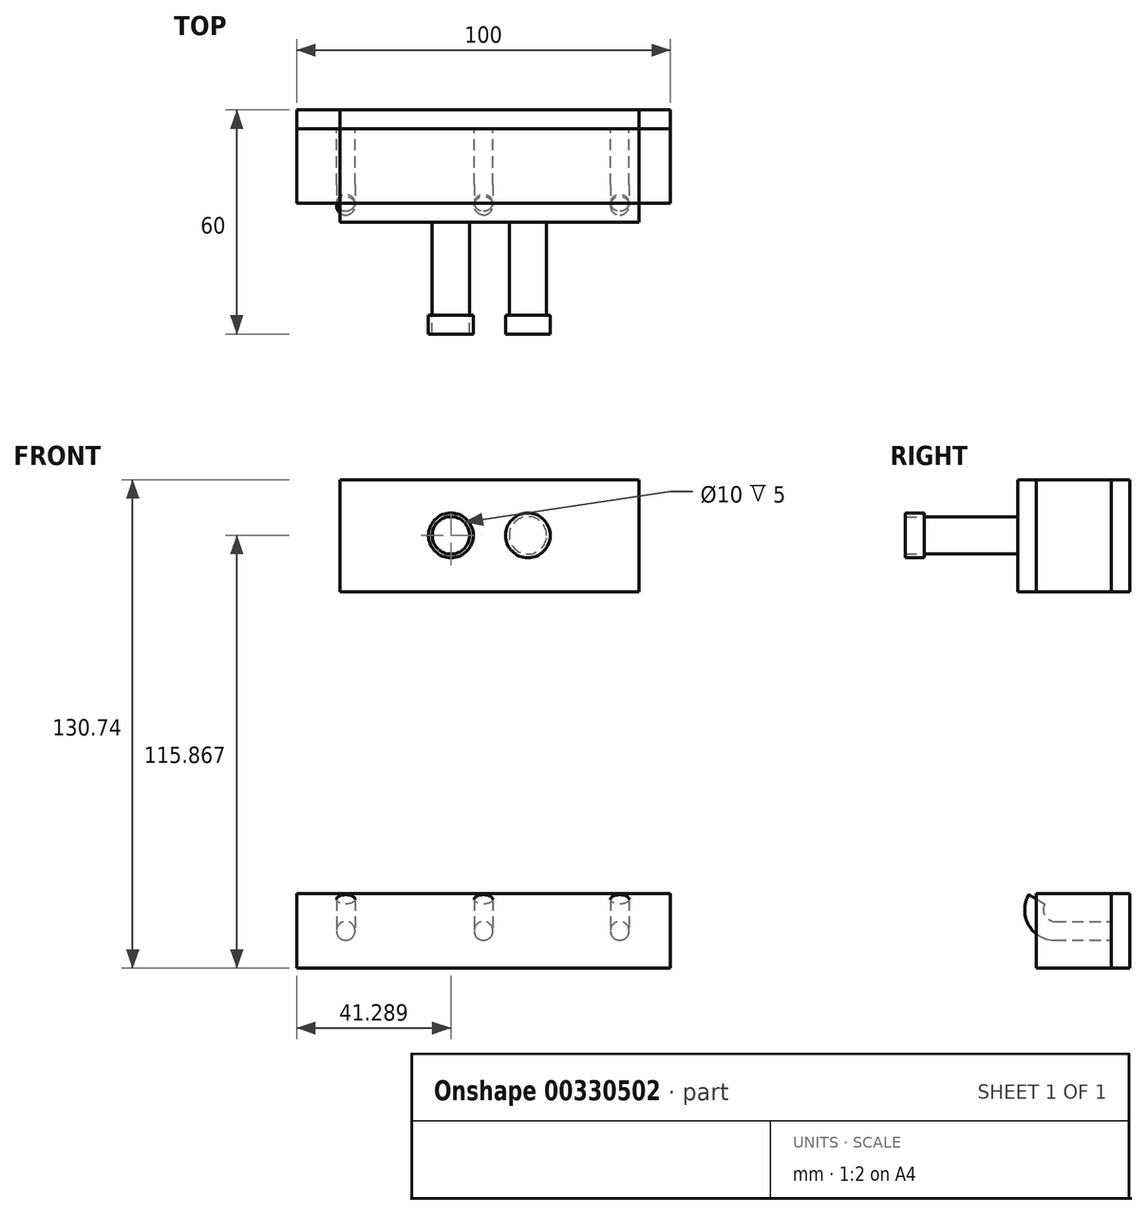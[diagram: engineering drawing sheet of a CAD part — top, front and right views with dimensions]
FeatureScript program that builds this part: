
annotation { "Feature Type Name" : "Feature", "Feature Type Description" : "" }
export const myFeature = defineFeature(function(context is Context, id is Id, definition is map)
    precondition{}
    {
        {
            var Q0;
            Q0=qCreatedBy(makeId("Front.planeOp"),FACE);
            var sketch = newSketch(context, id + "F0", { "sketchPlane" : qUnion([Q0])});
            skLineSegment(sketch, "E0.bottom", {"start": v(50, 10) * mm, "end": v(-50, 10) * mm});
            skLineSegment(sketch, "E0.top", {"start": v(50, -10) * mm, "end": v(-50, -10) * mm});
            skLineSegment(sketch, "E0.left", {"start": v(50, 10) * mm, "end": v(50, -10) * mm});
            skLineSegment(sketch, "E0.right", {"start": v(-50, 10) * mm, "end": v(-50, -10) * mm});
            skPoint(sketch, "E0.middle", {"position": v(0, 0) * mm});
            skLineSegment(sketch, "E1", {"start": v(-38.43, 120.74) * mm, "end": v(41.57, 120.74) * mm});
            skLineSegment(sketch, "E2", {"start": v(41.57, 120.74) * mm, "end": v(41.57, 90.74) * mm});
            skLineSegment(sketch, "E3", {"start": v(41.57, 90.74) * mm, "end": v(-38.43, 90.74) * mm});
            skLineSegment(sketch, "E4", {"start": v(-38.43, 90.74) * mm, "end": v(-38.43, 120.74) * mm});
            skSolve(sketch);
        }
        {
            var Q0;
            Q0 = qSketchRegion(id + "F0", true);
            extrude(context, id + "F1", {"entities" : qUnion([Q0]), "depth" : 5 * mm});
        }
        {
            var Q0;
            Q0=makeQuery(id+"F1.opExtrude","CAP_FACE",FACE,{"disambiguationData":[OSD([sQuery(id+"F0.wireOp",EDGE,"E0.bottom"),sQuery(id+"F0.wireOp",EDGE,"E0.top"),sQuery(id+"F0.wireOp",EDGE,"E0.left"),sQuery(id+"F0.wireOp",EDGE,"E0.right")])],"isStart":false});
            var sketch = newSketch(context, id + "F2", { "sketchPlane" : qUnion([Q0])});
            skCircle(sketch, "E5", {"center": v(0, 0) * mm, "radius": 2.5 * mm});
            skCircle(sketch, "E6", {"center": v(-36.85, 0) * mm, "radius": 2.5 * mm});
            skCircle(sketch, "E7", {"center": v(36.47, 0) * mm, "radius": 2.5 * mm});
            skSolve(sketch);
        }
        {
            var Q0;
            Q0=makeQuery(id+"F2.imprint","IMPRINT",FACE,{"disambiguationData":[TD([[makeQuery(id+"F2.imprint","IMPRINT",EDGE,{"derivedFrom":sQuery(id+"F2.wireOp",EDGE,"E5")}),1.0]])]});
            var Q1;
            Q1=makeQuery(id+"F2.imprint","IMPRINT",FACE,{"disambiguationData":[TD([[makeQuery(id+"F2.imprint","IMPRINT",EDGE,{"derivedFrom":sQuery(id+"F2.wireOp",EDGE,"E6")}),1.0]])]});
            var Q2;
            Q2=makeQuery(id+"F2.imprint","IMPRINT",FACE,{"disambiguationData":[TD([[makeQuery(id+"F2.imprint","IMPRINT",EDGE,{"derivedFrom":sQuery(id+"F2.wireOp",EDGE,"E7")}),1.0]])]});
            var Q3;
            Q3=sQuery(id+"F2.wireOp",EDGE,"E5");
            var Q4;
            Q4=sQuery(id+"F2.wireOp",EDGE,"E6");
            var Q5;
            Q5=sQuery(id+"F2.wireOp",EDGE,"E7");
            extrude(context, id + "F3", {"entities" : qUnion([Q0, Q1, Q2]), "operationType" : NewBodyOperationType.ADD, "surfaceEntities" : qUnion([Q3, Q4, Q5]), "depth" : 15 * mm});
        }
        {
            var Q0;
            Q0=makeQuery(id+"F3.opExtrude","CAP_FACE",FACE,{"disambiguationData":[OSD([sQuery(id+"F2.wireOp",EDGE,"E6")])],"isStart":false});
            var sketch = newSketch(context, id + "F4", { "sketchPlane" : qUnion([Q0])});
            skLineSegment(sketch, "E8", {"start": v(-44.61, 5.63) * mm, "end": v(45.39, 5.63) * mm});
            skSolve(sketch);
        }
        {
            var Q0;
            Q0=makeQuery(id+"F4.imprint","IMPRINT",FACE,{"disambiguationData":[TD([[makeQuery(id+"F4.imprint","IMPRINT",EDGE,{"derivedFrom":makeQuery(id+"F3.opExtrude","CAP_EDGE",EDGE,{"disambiguationData":[OSD([sQuery(id+"F2.wireOp",EDGE,"E6")])],"isStart":false})}),1.0]])]});
            var Q1;
            Q1=makeQuery(id+"F3.opExtrude","CAP_EDGE",EDGE,{"disambiguationData":[OSD([sQuery(id+"F2.wireOp",EDGE,"E6")])],"isStart":false});
            var Q2;
            Q2=sQuery(id+"F4.wireOp",EDGE,"E8");
            revolve(context, id + "F5", {"operationType" : NewBodyOperationType.ADD, "entities" : qUnion([Q0]), "surfaceEntities" : qUnion([Q1]), "axis" : qUnion([Q2]), "revolveType" : RevolveType.ONE_DIRECTION, "oppositeDirection" : true, "angle" : 120 * degree});
        }
        {
            var Q0;
            Q0=makeQuery(id+"F3.opExtrude","CAP_FACE",FACE,{"disambiguationData":[OSD([sQuery(id+"F2.wireOp",EDGE,"E5")])],"isStart":false});
            var Q1;
            Q1=makeQuery(id+"F3.opExtrude","CAP_EDGE",EDGE,{"disambiguationData":[OSD([sQuery(id+"F2.wireOp",EDGE,"E5")])],"isStart":false});
            var Q2;
            Q2=sQuery(id+"F4.wireOp",EDGE,"E8");
            revolve(context, id + "F6", {"operationType" : NewBodyOperationType.ADD, "entities" : qUnion([Q0]), "surfaceEntities" : qUnion([Q1]), "axis" : qUnion([Q2]), "revolveType" : RevolveType.ONE_DIRECTION, "oppositeDirection" : true, "angle" : 120 * degree});
        }
        {
            var Q0;
            Q0=makeQuery(id+"F3.opExtrude","CAP_FACE",FACE,{"disambiguationData":[OSD([sQuery(id+"F2.wireOp",EDGE,"E7")])],"isStart":false});
            var Q1;
            Q1=makeQuery(id+"F3.opExtrude","CAP_EDGE",EDGE,{"disambiguationData":[OSD([sQuery(id+"F2.wireOp",EDGE,"E7")])],"isStart":false});
            var Q2;
            Q2=sQuery(id+"F4.wireOp",EDGE,"E8");
            revolve(context, id + "F7", {"operationType" : NewBodyOperationType.ADD, "entities" : qUnion([Q0]), "surfaceEntities" : qUnion([Q1]), "axis" : qUnion([Q2]), "revolveType" : RevolveType.ONE_DIRECTION, "oppositeDirection" : true, "angle" : 120 * degree});
        }
        {
            var Q0;
            Q0 = qSketchRegion(id + "F0", true);
            var Q1;
            Q1=makeQuery(id+"F1.opExtrude","CAP_FACE",FACE,{"disambiguationData":[OSD([sQuery(id+"F0.wireOp",EDGE,"E1"),sQuery(id+"F0.wireOp",EDGE,"E2"),sQuery(id+"F0.wireOp",EDGE,"E3"),sQuery(id+"F0.wireOp",EDGE,"E4")])],"isStart":false});
            extrude(context, id + "F8", {"entities" : qUnion([Q0, Q1]), "depth" : 25 * mm});
        }
        {
            var Q0;
            {var subQ0=sQuery(id+"F0.wireOp",EDGE,"E4");var subQ1=sQuery(id+"F0.wireOp",EDGE,"E3");var subQ2=sQuery(id+"F0.wireOp",EDGE,"E2");var subQ3=sQuery(id+"F0.wireOp",EDGE,"E1");Q0=makeQuery(id+"F8.opExtrude","CAP_FACE",FACE,{"disambiguationData":[OSD([subQ3,subQ2,subQ1,subQ0]),TDD([makeQuery(id+"F1.opExtrude","CAP_FACE",FACE,{"disambiguationData":[OSD([subQ3,subQ2,subQ1,subQ0])],"isStart":false})])],"isStart":false});}
            var sketch = newSketch(context, id + "F9", { "sketchPlane" : qUnion([Q0])});
            skLineSegment(sketch, "E9", {"start": v(41.57, 120.74) * mm, "end": v(11.57, 120.74) * mm});
            skLineSegment(sketch, "E10", {"start": v(11.57, 120.74) * mm, "end": v(11.57, 90.74) * mm});
            skSolve(sketch);
        }
        {
            var Q0;
            {var subQ0=sQuery(id+"F9.wireOp",EDGE,"E10");Q0=makeQuery(id+"F9.imprint","IMPRINT",FACE,{"disambiguationData":[TD([[makeQuery(id+"F9.imprint","IMPRINT",EDGE,{"derivedFrom":subQ0}),-1.0]])]});}
            var sketch = newSketch(context, id + "F10", { "sketchPlane" : qUnion([Q0])});
            skCircle(sketch, "E11", {"center": v(-8.71, 105.87) * mm, "radius": 5 * mm});
            skCircle(sketch, "E12", {"center": v(11.89, 105.87) * mm, "radius": 5 * mm});
            skSolve(sketch);
        }
        {
            var Q0;
            {var subQ0=sQuery(id+"F10.wireOp",EDGE,"E12");var subQ1=makeQuery(id+"F9.imprint","IMPRINT",EDGE,{"derivedFrom":sQuery(id+"F9.wireOp",EDGE,"E10")});var subQ2=makeQuery(id+"F10.imprint","INTERSECT",VERTEX,{"disambiguationData":[OD(0.0)],"derivedFrom":[subQ1,subQ0]});Q0=makeQuery(id+"F10.imprint","IMPRINT",FACE,{"disambiguationData":[TD([[makeQuery(id+"F10.imprint","IMPRINT",EDGE,{"disambiguationData":[TD([[subQ2,-1.0]])],"derivedFrom":subQ0}),1.0]])]});}
            var Q1;
            {var subQ0=sQuery(id+"F10.wireOp",EDGE,"E12");var subQ1=makeQuery(id+"F9.imprint","IMPRINT",EDGE,{"derivedFrom":sQuery(id+"F9.wireOp",EDGE,"E10")});var subQ2=makeQuery(id+"F10.imprint","INTERSECT",VERTEX,{"disambiguationData":[OD(0.0)],"derivedFrom":[subQ1,subQ0]});Q1=makeQuery(id+"F10.imprint","IMPRINT",FACE,{"disambiguationData":[TD([[makeQuery(id+"F10.imprint","IMPRINT",EDGE,{"disambiguationData":[TD([[subQ2,1.0]])],"derivedFrom":subQ0}),1.0]])]});}
            var Q2;
            Q2=makeQuery(id+"F10.imprint","IMPRINT",FACE,{"disambiguationData":[TD([[makeQuery(id+"F10.imprint","IMPRINT",EDGE,{"derivedFrom":sQuery(id+"F10.wireOp",EDGE,"E11")}),1.0]])]});
            extrude(context, id + "F11", {"entities" : qUnion([Q0, Q1, Q2]), "operationType" : NewBodyOperationType.ADD, "depth" : 25 * mm});
        }
        {
            var Q0;
            Q0=makeQuery(id+"F11.opExtrude","CAP_FACE",FACE,{"disambiguationData":[OSD([sQuery(id+"F10.wireOp",EDGE,"E12")])],"isStart":false});
            var sketch = newSketch(context, id + "F12", { "sketchPlane" : qUnion([Q0])});
            skCircle(sketch, "E13", {"center": v(11.89, 105.87) * mm, "radius": 6 * mm});
            skCircle(sketch, "E14", {"center": v(-8.5, 105.87) * mm, "radius": 6 * mm});
            skSolve(sketch);
        }
        {
            var Q0;
            Q0=makeQuery(id+"F12.imprint","IMPRINT",FACE,{"disambiguationData":[TD([[makeQuery(id+"F12.imprint","IMPRINT",EDGE,{"derivedFrom":sQuery(id+"F12.wireOp",EDGE,"E13")}),1.0]])]});
            var Q1;
            Q1=makeQuery(id+"F12.imprint","IMPRINT",FACE,{"disambiguationData":[TD([[makeQuery(id+"F12.imprint","IMPRINT",EDGE,{"derivedFrom":makeQuery(id+"F11.opExtrude","CAP_EDGE",EDGE,{"disambiguationData":[OSD([sQuery(id+"F10.wireOp",EDGE,"E12")])],"isStart":false})}),1.0]])]});
            extrude(context, id + "F13", {"entities" : qUnion([Q0, Q1]), "operationType" : NewBodyOperationType.ADD, "depth" : 5 * mm});
        }
        {
            var Q0;
            Q0=makeQuery(id+"F11.opExtrude","CAP_FACE",FACE,{"disambiguationData":[OSD([sQuery(id+"F10.wireOp",EDGE,"E11")])],"isStart":false});
            var sketch = newSketch(context, id + "F14", { "sketchPlane" : qUnion([Q0])});
            skCircle(sketch, "E15", {"center": v(-8.71, 105.87) * mm, "radius": 6 * mm});
            skSolve(sketch);
        }
        {
            var Q0;
            Q0=makeQuery(id+"F14.imprint","IMPRINT",FACE,{"disambiguationData":[TD([[makeQuery(id+"F14.imprint","IMPRINT",EDGE,{"derivedFrom":makeQuery(id+"F11.opExtrude","CAP_EDGE",EDGE,{"disambiguationData":[OSD([sQuery(id+"F10.wireOp",EDGE,"E11")])],"isStart":false})}),1.0]])]});
            var sketch = newSketch(context, id + "F15", { "sketchPlane" : qUnion([Q0])});
            skSolve(sketch);
        }
        {
            var Q0;
            Q0=makeQuery(id+"F14.imprint","IMPRINT",FACE,{"disambiguationData":[TD([[makeQuery(id+"F14.imprint","IMPRINT",EDGE,{"derivedFrom":sQuery(id+"F14.wireOp",EDGE,"E15")}),1.0]])]});
            extrude(context, id + "F16", {"entities" : qUnion([Q0]), "depth" : 5 * mm});
        }
    });
